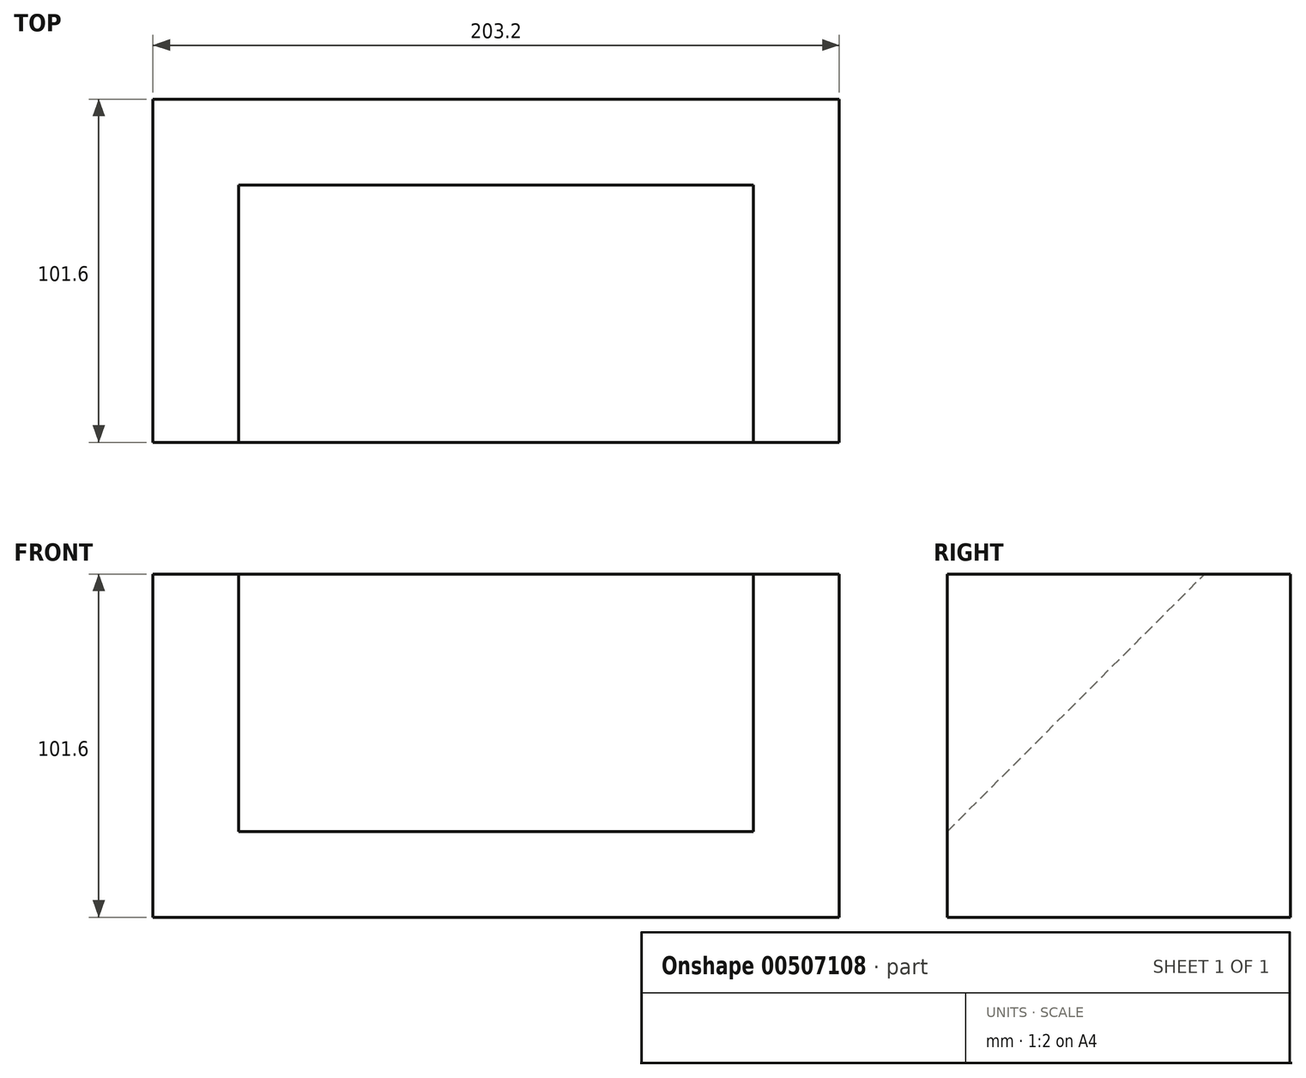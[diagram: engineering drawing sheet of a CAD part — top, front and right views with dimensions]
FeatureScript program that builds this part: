
annotation { "Feature Type Name" : "Feature", "Feature Type Description" : "" }
export const myFeature = defineFeature(function(context is Context, id is Id, definition is map)
    precondition{}
    {
        {
            var Q0;
            Q0=qCreatedBy(makeId("Right.planeOp"),FACE);
            var sketch = newSketch(context, id + "F0", { "sketchPlane" : qUnion([Q0])});
            skLineSegment(sketch, "E0", {"start": v(0, 0) * mm, "end": v(101.6, 0) * mm});
            skLineSegment(sketch, "E1", {"start": v(101.6, 0) * mm, "end": v(101.6, 101.6) * mm});
            skLineSegment(sketch, "E2", {"start": v(101.6, 101.6) * mm, "end": v(0, 101.6) * mm});
            skLineSegment(sketch, "E3", {"start": v(0, 101.6) * mm, "end": v(0, 0) * mm});
            skSolve(sketch);
        }
        {
            var Q0;
            Q0=makeQuery(id+"F0.imprint","IMPRINT",FACE,{"disambiguationData":[TD([[makeQuery(id+"F0.imprint","IMPRINT",EDGE,{"derivedFrom":sQuery(id+"F0.wireOp",EDGE,"E0")}),1.0]])]});
            extrude(context, id + "F1", {"entities" : qUnion([Q0]), "oppositeDirection" : true, "depth" : 25.4 * mm});
        }
        {
            var Q0;
            Q0=makeQuery(id+"F1.opExtrude","CAP_FACE",FACE,{"disambiguationData":[OSD([sQuery(id+"F0.wireOp",EDGE,"E0"),sQuery(id+"F0.wireOp",EDGE,"E1"),sQuery(id+"F0.wireOp",EDGE,"E2"),sQuery(id+"F0.wireOp",EDGE,"E3")])],"isStart":false});
            var sketch = newSketch(context, id + "F2", { "sketchPlane" : qUnion([Q0])});
            skLineSegment(sketch, "E4", {"start": v(0, 0) * mm, "end": v(-101.6, 0) * mm});
            skLineSegment(sketch, "E5", {"start": v(-101.6, 0) * mm, "end": v(-101.6, 101.6) * mm});
            skLineSegment(sketch, "E6", {"start": v(-101.6, 101.6) * mm, "end": v(-76.2, 101.6) * mm});
            skLineSegment(sketch, "E7", {"start": v(0, 0) * mm, "end": v(0, 25.4) * mm});
            skLineSegment(sketch, "E8", {"start": v(0, 25.4) * mm, "end": v(-76.2, 101.6) * mm});
            skSolve(sketch);
        }
        {
            var Q0;
            Q0=makeQuery(id+"F2.imprint","IMPRINT",FACE,{"disambiguationData":[TD([[makeQuery(id+"F2.imprint","IMPRINT",EDGE,{"derivedFrom":sQuery(id+"F2.wireOp",EDGE,"E4")}),-1.0]])]});
            extrude(context, id + "F3", {"entities" : qUnion([Q0]), "operationType" : NewBodyOperationType.ADD, "depth" : 152.4 * mm});
        }
        {
            var Q0;
            Q0=makeQuery(id+"F3.opExtrude","CAP_FACE",FACE,{"disambiguationData":[OSD([sQuery(id+"F2.wireOp",EDGE,"E4"),sQuery(id+"F2.wireOp",EDGE,"E5"),sQuery(id+"F2.wireOp",EDGE,"E6"),sQuery(id+"F2.wireOp",EDGE,"E7"),sQuery(id+"F2.wireOp",EDGE,"E8")])],"isStart":false});
            var sketch = newSketch(context, id + "F4", { "sketchPlane" : qUnion([Q0])});
            skLineSegment(sketch, "E9", {"start": v(0, 0) * mm, "end": v(-101.6, 0) * mm});
            skLineSegment(sketch, "E10", {"start": v(-101.6, 0) * mm, "end": v(-101.6, 101.6) * mm});
            skSolve(sketch);
        }
        {
            var Q0;
            Q0=makeQuery(id+"F4.imprint","IMPRINT",FACE,{"disambiguationData":[TD([[makeQuery(id+"F4.imprint","IMPRINT",EDGE,{"derivedFrom":sQuery(id+"F4.wireOp",EDGE,"E9")}),-1.0]])]});
            var sketch = newSketch(context, id + "F5", { "sketchPlane" : qUnion([Q0])});
            skLineSegment(sketch, "E11", {"start": v(0, 0) * mm, "end": v(-101.6, 0) * mm});
            skLineSegment(sketch, "E12", {"start": v(-101.6, 0) * mm, "end": v(-101.6, 101.6) * mm});
            skLineSegment(sketch, "E13", {"start": v(-101.6, 101.6) * mm, "end": v(0, 101.6) * mm});
            skLineSegment(sketch, "E14", {"start": v(0, 101.6) * mm, "end": v(0, 0) * mm});
            skSolve(sketch);
        }
        {
            var Q0;
            {var subQ1=makeQuery(id+"F4.imprint","IMPRINT",EDGE,{"derivedFrom":makeQuery(id+"F3.opExtrude","CAP_EDGE",EDGE,{"disambiguationData":[OSD([sQuery(id+"F2.wireOp",EDGE,"E8")])],"isStart":false})});Q0=makeQuery(id+"F5.imprint","IMPRINT",FACE,{"disambiguationData":[TD([[makeQuery(id+"F5.imprint","IMPRINT",EDGE,{"derivedFrom":subQ1}),-1.0]])]});}
            var Q1;
            Q1=makeQuery(id+"F4.imprint","IMPRINT",FACE,{"disambiguationData":[TD([[makeQuery(id+"F4.imprint","IMPRINT",EDGE,{"derivedFrom":sQuery(id+"F4.wireOp",EDGE,"E9")}),-1.0]])]});
            extrude(context, id + "F6", {"entities" : qUnion([Q0, Q1]), "operationType" : NewBodyOperationType.ADD, "depth" : 25.4 * mm});
        }
    });
